# Revit family: IS_Simplicicty_E1317_BIM_FR
name_source: partatom
category: Plumbing Fixtures
revit_build: Autodesk Revit 2017 (Build: 20160225_1515(x64)
units: mm (PartAtom-declared; Revit-internal decimal feet)

## family parameters
Cut with Voids When Loaded = No
Host = Face
OmniClass Number = 23.45.05.21.11.11
OmniClass Title = Water Operated Water Closets
Part Type = Normal
Room Calculation Point = No
Round Connector Dimension = Use Diameter
Shared = No

## types (1)
- E131701 - SIMPLICITY SEDATKO
    Accessoires = www.idealstandard.be
    Assembly Code = C1030200
    Bim-NomDuProjet = ISI_IdealStandard_Simplicicty_E1317
    Caractéristiques = Abattant. Thermodur (En Urea). A Charnières Inox. 
Fixation Dessus
    CodeBarre = 5017830525875
    ConseilsDInstallation = www.idealstandard.be
    Cost = 0 $
    Couleur = Blanc
    CoûtDeRemplacement = 0
    DateDeCréation = 2018_08_15
    Default Elevation = 0 mm  [stored 0 ft]
    Description = Abattant. Thermodur (En Urea). A Charnières Inox. 
Fixation Dessus
    Dimensions = 40 x 365 x 443 mm
    Espace = Interne
    Finition = Blanc
    Forme = Complexe
    Hauteur = 40 mm  [stored 0.131234 ft]
    IfcExportAs = IfcSanitaryTerminalType
    IfcExportType = WCSEATS
    InformationsProduit = www.idealstandard.be
    Largeur = 365 mm  [stored 1.19751 ft]
    LienUtile = www.idealstandard.be
    Longueur = 443 mm  [stored 1.45341 ft]
    Manufacturer = www.idealstandard.be
    Marque = Ideal Standard
    Matériel = Plastique
    Model = E131701
    PoidsNet = 0
    Profondeur = 0 mm  [stored 0 ft]
    Raccordement = Plomberie
    Révision = 1
    URL = www.idealstandard.be
    Uniclass2015Code = Pr_40_20_93_95
    Uniclass2015Title = WC seats and covers
    UnitéDeMesure = Millimètres
    UnitéDeTemps = An
    UnitéMonétaire = €
    UrlDuFabricant = www.idealstandard.be

note: [stored X ft] marks values corroborated as IEEE doubles in the binary element streams (Revit-internal decimal feet)

## geometry (parser evidence)
native form markers: Sweep x3
no freeform markers — native parametric forms only
